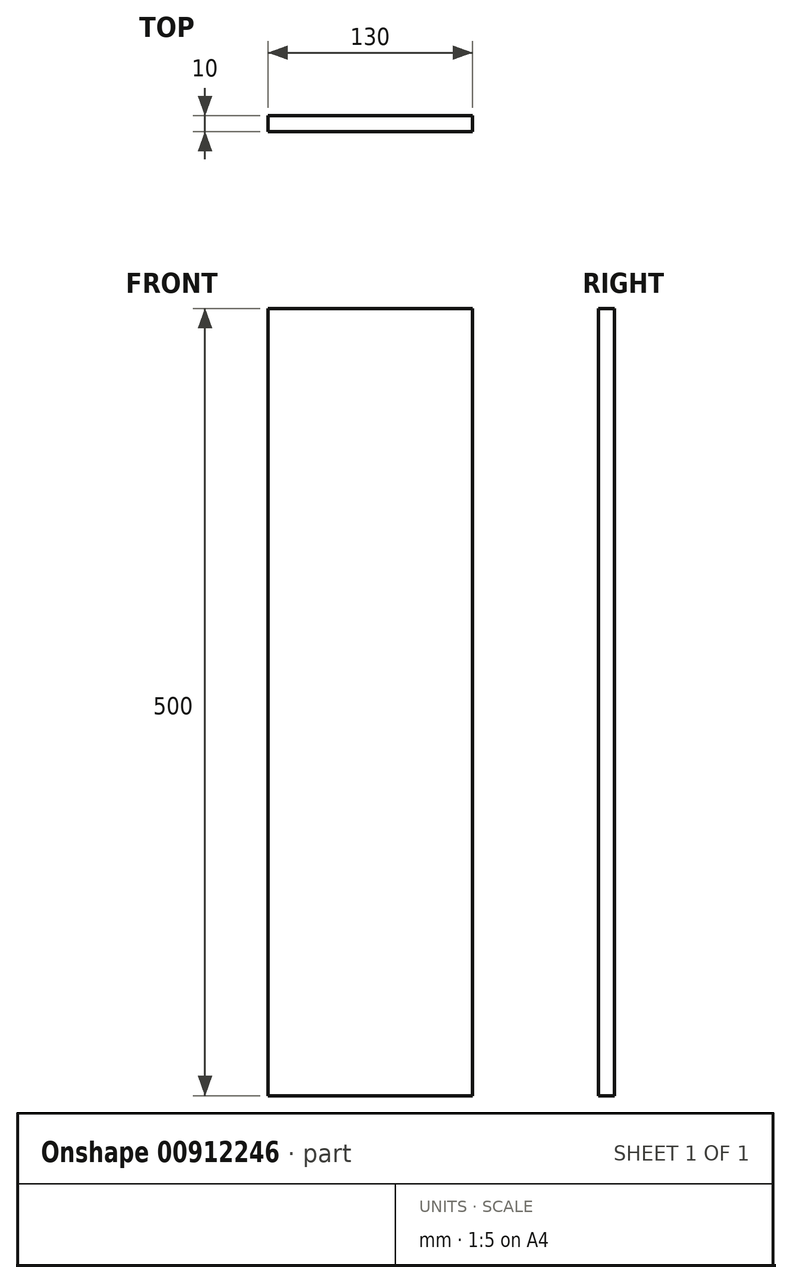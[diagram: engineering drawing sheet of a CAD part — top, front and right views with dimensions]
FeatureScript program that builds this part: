
annotation { "Feature Type Name" : "Feature", "Feature Type Description" : "" }
export const myFeature = defineFeature(function(context is Context, id is Id, definition is map)
    precondition{}
    {
        {
            var Q0;
            Q0=qCreatedBy(makeId("Front.planeOp"),FACE);
            var sketch = newSketch(context, id + "F0", { "sketchPlane" : qUnion([Q0])});
            skLineSegment(sketch, "E0.bottom", {"start": v(-68.95, 461.68) * mm, "end": v(61.05, 461.68) * mm});
            skLineSegment(sketch, "E0.top", {"start": v(-68.95, -38.32) * mm, "end": v(61.05, -38.32) * mm});
            skLineSegment(sketch, "E0.left", {"start": v(-68.95, 461.68) * mm, "end": v(-68.95, -38.32) * mm});
            skLineSegment(sketch, "E0.right", {"start": v(61.05, 461.68) * mm, "end": v(61.05, -38.32) * mm});
            skSolve(sketch);
        }
        {
            var Q0;
            Q0=makeQuery(id+"F0.imprint","IMPRINT",FACE,{"disambiguationData":[TD([[makeQuery(id+"F0.imprint","IMPRINT",EDGE,{"derivedFrom":sQuery(id+"F0.wireOp",EDGE,"E0.bottom")}),-1.0]])]});
            extrude(context, id + "F1", {"entities" : qUnion([Q0]), "depth" : 10 * mm, "offsetDistance" : 25 * mm});
        }
    });
